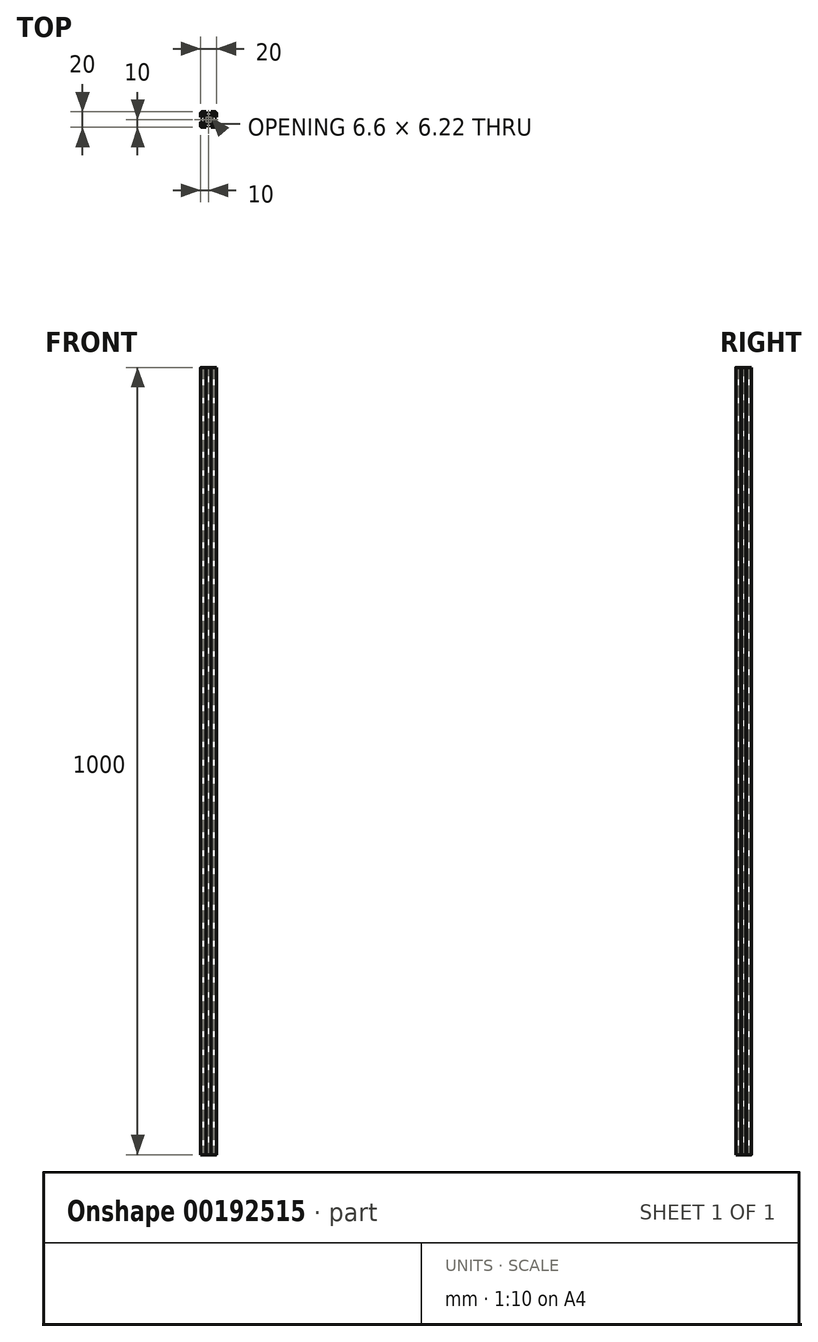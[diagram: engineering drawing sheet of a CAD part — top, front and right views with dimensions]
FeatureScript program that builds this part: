
annotation { "Feature Type Name" : "Feature", "Feature Type Description" : "" }
export const myFeature = defineFeature(function(context is Context, id is Id, definition is map)
    precondition{}
    {
        {
            var Q0;
            Q0=qCreatedBy(makeId("Top.planeOp"),FACE);
            var sketch = newSketch(context, id + "F0", { "sketchPlane" : qUnion([Q0])});
            skLineSegment(sketch, "E0.bottom", {"start": v(-10, 10) * mm, "end": v(10, 10) * mm});
            skLineSegment(sketch, "E0.top", {"start": v(-10, -10) * mm, "end": v(10, -10) * mm});
            skLineSegment(sketch, "E0.left", {"start": v(-10, 10) * mm, "end": v(-10, -10) * mm});
            skLineSegment(sketch, "E0.right", {"start": v(10, 10) * mm, "end": v(10, -10) * mm});
            skSolve(sketch);
        }
        {
            var Q0;
            Q0 = qSketchRegion(id + "F0", true);
            extrude(context, id + "F1", {"entities" : qUnion([Q0]), "depth" : 1000 * mm});
        }
        {
            var Q0;
            Q0=makeQuery(id+"F1.opExtrude","SWEPT_EDGE",EDGE,{"disambiguationData":[OSD([sQuery(id+"F0.wireOp",EDGE,"E0.bottom"),sQuery(id+"F0.wireOp",EDGE,"E0.right")])]});
            var Q1;
            Q1=makeQuery(id+"F1.opExtrude","SWEPT_EDGE",EDGE,{"disambiguationData":[OSD([sQuery(id+"F0.wireOp",EDGE,"E0.bottom"),sQuery(id+"F0.wireOp",EDGE,"E0.left")])]});
            var Q2;
            Q2=makeQuery(id+"F1.opExtrude","SWEPT_EDGE",EDGE,{"disambiguationData":[OSD([sQuery(id+"F0.wireOp",EDGE,"E0.top"),sQuery(id+"F0.wireOp",EDGE,"E0.left")])]});
            var Q3;
            Q3=makeQuery(id+"F1.opExtrude","SWEPT_EDGE",EDGE,{"disambiguationData":[OSD([sQuery(id+"F0.wireOp",EDGE,"E0.top"),sQuery(id+"F0.wireOp",EDGE,"E0.right")])]});
            fillet(context, id + "F2", {"entities" : qUnion([Q0, Q1, Q2, Q3]), "radius" : 2 * mm, "tangentPropagation" : true, "allowEdgeOverflow" : false});
        }
        {
            var Q0;
            Q0=makeQuery(id+"F1.opExtrude","CAP_FACE",FACE,{"disambiguationData":[OSD([sQuery(id+"F0.wireOp",EDGE,"E0.bottom"),sQuery(id+"F0.wireOp",EDGE,"E0.top"),sQuery(id+"F0.wireOp",EDGE,"E0.left"),sQuery(id+"F0.wireOp",EDGE,"E0.right")])],"isStart":true});
            var sketch = newSketch(context, id + "F3", { "sketchPlane" : qUnion([Q0])});
            skLineSegment(sketch, "E1", {"start": v(-10, 3) * mm, "end": v(-8.5, 3) * mm});
            skLineSegment(sketch, "E2", {"start": v(-8.5, 3) * mm, "end": v(-8.5, 5.63) * mm});
            skLineSegment(sketch, "E3", {"start": v(-8.5, 5.63) * mm, "end": v(-7.13, 5.63) * mm});
            skLineSegment(sketch, "E4", {"start": v(-7.13, 5.63) * mm, "end": v(-4.5, 3) * mm});
            skLineSegment(sketch, "E5", {"start": v(-4.5, 3) * mm, "end": v(-4.5, 0) * mm});
            skLineSegment(sketch, "E6.MirrorCS", {"start": v(-8.5, -5.63) * mm, "end": v(-7.13, -5.63) * mm});
            skLineSegment(sketch, "E7.MirrorCS", {"start": v(-10, -3) * mm, "end": v(-8.5, -3) * mm});
            skLineSegment(sketch, "E8.MirrorCS", {"start": v(-8.5, -3) * mm, "end": v(-8.5, -5.63) * mm});
            skLineSegment(sketch, "E9.MirrorCS", {"start": v(-7.13, -5.63) * mm, "end": v(-4.5, -3) * mm});
            skLineSegment(sketch, "E10.MirrorCS", {"start": v(-4.5, -3) * mm, "end": v(-4.5, 0) * mm});
            skLineSegment(sketch, "E11", {"start": v(0, 15.03) * mm, "end": v(0, -14.36) * mm, "construction": true});
            skLineSegment(sketch, "E12.MirrorCS", {"start": v(8.5, 5.63) * mm, "end": v(7.13, 5.63) * mm});
            skLineSegment(sketch, "E13.MirrorCS", {"start": v(8.5, -5.63) * mm, "end": v(7.13, -5.63) * mm});
            skLineSegment(sketch, "E14.MirrorCS", {"start": v(10, 3) * mm, "end": v(8.5, 3) * mm});
            skLineSegment(sketch, "E15.MirrorCS", {"start": v(8.5, 3) * mm, "end": v(8.5, 5.63) * mm});
            skLineSegment(sketch, "E16.MirrorCS", {"start": v(10, -3) * mm, "end": v(8.5, -3) * mm});
            skLineSegment(sketch, "E17.MirrorCS", {"start": v(7.13, 5.63) * mm, "end": v(4.5, 3) * mm});
            skLineSegment(sketch, "E18.MirrorCS", {"start": v(4.5, -3) * mm, "end": v(4.5, 0) * mm});
            skLineSegment(sketch, "E19.MirrorCS", {"start": v(7.13, -5.63) * mm, "end": v(4.5, -3) * mm});
            skLineSegment(sketch, "E20.MirrorCS", {"start": v(4.5, 3) * mm, "end": v(4.5, 0) * mm});
            skLineSegment(sketch, "E21.MirrorCS", {"start": v(8.5, -3) * mm, "end": v(8.5, -5.63) * mm});
            skLineSegment(sketch, "E22", {"start": v(-9.41, 9.41) * mm, "end": v(3, -3) * mm, "construction": true});
            skLineSegment(sketch, "E23.MirrorCS", {"start": v(-5.63, -8.5) * mm, "end": v(-5.63, -7.13) * mm});
            skLineSegment(sketch, "E24.MirrorCS", {"start": v(5.63, -8.5) * mm, "end": v(5.63, -7.13) * mm});
            skLineSegment(sketch, "E25.MirrorCS", {"start": v(-3, -10) * mm, "end": v(-3, -8.5) * mm});
            skLineSegment(sketch, "E26.MirrorCS", {"start": v(3, -10) * mm, "end": v(3, -8.5) * mm});
            skLineSegment(sketch, "E27.MirrorCS", {"start": v(-5.63, -7.13) * mm, "end": v(-3, -4.5) * mm});
            skLineSegment(sketch, "E28.MirrorCS", {"start": v(-3, -8.5) * mm, "end": v(-5.63, -8.5) * mm});
            skLineSegment(sketch, "E29.MirrorCS", {"start": v(3, -8.5) * mm, "end": v(5.63, -8.5) * mm});
            skLineSegment(sketch, "E30.MirrorCS", {"start": v(3, -4.5) * mm, "end": v(0, -4.5) * mm});
            skLineSegment(sketch, "E31.MirrorCS", {"start": v(-3, -4.5) * mm, "end": v(0, -4.5) * mm});
            skLineSegment(sketch, "E32.MirrorCS", {"start": v(5.63, -7.13) * mm, "end": v(3, -4.5) * mm});
            skLineSegment(sketch, "E33.MirrorCS", {"start": v(-15.03, 0) * mm, "end": v(14.36, 0) * mm, "construction": true});
            skLineSegment(sketch, "E34.MirrorCS", {"start": v(5.63, 7.13) * mm, "end": v(3, 4.5) * mm});
            skLineSegment(sketch, "E35.MirrorCS", {"start": v(-5.63, 7.13) * mm, "end": v(-3, 4.5) * mm});
            skLineSegment(sketch, "E36.MirrorCS", {"start": v(-3, 4.5) * mm, "end": v(0, 4.5) * mm});
            skLineSegment(sketch, "E37.MirrorCS", {"start": v(3, 4.5) * mm, "end": v(0, 4.5) * mm});
            skLineSegment(sketch, "E38.MirrorCS", {"start": v(-5.63, 8.5) * mm, "end": v(-5.63, 7.13) * mm});
            skLineSegment(sketch, "E39.MirrorCS", {"start": v(5.63, 8.5) * mm, "end": v(5.63, 7.13) * mm});
            skLineSegment(sketch, "E40.MirrorCS", {"start": v(3, 10) * mm, "end": v(3, 8.5) * mm});
            skLineSegment(sketch, "E41.MirrorCS", {"start": v(-3, 10) * mm, "end": v(-3, 8.5) * mm});
            skLineSegment(sketch, "E42.MirrorCS", {"start": v(3, 8.5) * mm, "end": v(5.63, 8.5) * mm});
            skLineSegment(sketch, "E43.MirrorCS", {"start": v(-3, 8.5) * mm, "end": v(-5.63, 8.5) * mm});
            skSolve(sketch);
        }
        {
            var Q0;
            Q0 = qSketchRegion(id + "F3", true);
            var Q1;
            Q1=makeQuery(id+"F3.imprint","IMPRINT",FACE,{"disambiguationData":[TD([[makeQuery(id+"F3.imprint","IMPRINT",EDGE,{"derivedFrom":sQuery(id+"F3.wireOp",EDGE,"E35.MirrorCS")}),1.0]])]});
            var Q2;
            Q2=makeQuery(id+"F3.imprint","IMPRINT",FACE,{"disambiguationData":[TD([[makeQuery(id+"F3.imprint","IMPRINT",EDGE,{"derivedFrom":sQuery(id+"F3.wireOp",EDGE,"E20.MirrorCS")}),1.0]])]});
            var Q3;
            Q3=makeQuery(id+"F3.imprint","IMPRINT",FACE,{"disambiguationData":[TD([[makeQuery(id+"F3.imprint","IMPRINT",EDGE,{"derivedFrom":sQuery(id+"F3.wireOp",EDGE,"E23.MirrorCS")}),-1.0]])]});
            var Q4;
            {var subQ0=sQuery(id+"F3.wireOp",EDGE,"E1");Q4=makeQuery(id+"F3.imprint","IMPRINT",FACE,{"disambiguationData":[TD([[makeQuery(id+"F3.imprint","IMPRINT",EDGE,{"derivedFrom":subQ0}),-1.0]])]});}
            extrude(context, id + "F4", {"entities" : qUnion([Q0, Q1, Q2, Q3, Q4]), "operationType" : NewBodyOperationType.REMOVE, "endBound" : BoundingType.UP_TO_NEXT, "oppositeDirection" : true, "depth" : 25.4 * mm});
        }
        {
            var Q0;
            Q0=makeQuery(id+"F1.opExtrude","CAP_FACE",FACE,{"disambiguationData":[OSD([sQuery(id+"F0.wireOp",EDGE,"E0.bottom"),sQuery(id+"F0.wireOp",EDGE,"E0.top"),sQuery(id+"F0.wireOp",EDGE,"E0.left"),sQuery(id+"F0.wireOp",EDGE,"E0.right")])],"isStart":false});
            var sketch = newSketch(context, id + "F5", { "sketchPlane" : qUnion([Q0])});
            skArc(sketch, "E44", {"start": v(-2.68, -0.6) * mm, "mid": v(-2.38, -1.37) * mm, "end": v(-1.87, -2.02) * mm});
            skLineSegment(sketch, "E45", {"start": v(-7.32, 0) * mm, "end": v(15.13, 0) * mm, "construction": true});
            skPoint(sketch, "E45.endSnap0", {"position": v(-4.5, 0) * mm});
            skLineSegment(sketch, "E46", {"start": v(-3.3, 0.5) * mm, "end": v(-3.3, 0) * mm});
            skLineSegment(sketch, "E47", {"start": v(-3.3, 0.5) * mm, "end": v(-2.68, 0.6) * mm});
            skLineSegment(sketch, "E48.MirrorCS", {"start": v(-3.3, -0.5) * mm, "end": v(-2.68, -0.6) * mm});
            skLineSegment(sketch, "E49.MirrorCS", {"start": v(-3.3, -0.5) * mm, "end": v(-3.3, 0) * mm});
            skLineSegment(sketch, "E50", {"start": v(0, 3.17) * mm, "end": v(0, -3.5) * mm, "construction": true});
            skLineSegment(sketch, "E51.MirrorCS", {"start": v(3.3, -0.5) * mm, "end": v(2.68, -0.6) * mm});
            skLineSegment(sketch, "E52.MirrorCS", {"start": v(3.3, -0.5) * mm, "end": v(3.3, 0) * mm});
            skLineSegment(sketch, "E53.MirrorCS", {"start": v(3.3, 0.5) * mm, "end": v(2.68, 0.6) * mm});
            skLineSegment(sketch, "E54.MirrorCS", {"start": v(3.3, 0.5) * mm, "end": v(3.3, 0) * mm});
            skArc(sketch, "E55.trimOffspring", {"start": v(2.68, 0.6) * mm, "mid": v(2.38, 1.38) * mm, "end": v(1.87, 2.02) * mm});
            skLineSegment(sketch, "E56", {"start": v(-2.57, 4.46) * mm, "end": v(0, 0) * mm, "construction": true});
            skLineSegment(sketch, "E57", {"start": v(0, 0) * mm, "end": v(2.15, 3.72) * mm, "construction": true});
            skLineSegment(sketch, "E58.MirrorCS", {"start": v(-2.08, 2.6) * mm, "end": v(-1.87, 2.02) * mm});
            skLineSegment(sketch, "E59.MirrorCS", {"start": v(-2.08, 2.6) * mm, "end": v(-1.65, 2.86) * mm});
            skLineSegment(sketch, "E60.MirrorCS", {"start": v(-1.22, 3.1) * mm, "end": v(-0.81, 2.63) * mm});
            skLineSegment(sketch, "E61.MirrorCS", {"start": v(-1.22, 3.1) * mm, "end": v(-1.65, 2.86) * mm});
            skLineSegment(sketch, "E62.MirrorCS", {"start": v(2.08, -2.6) * mm, "end": v(1.87, -2.02) * mm});
            skLineSegment(sketch, "E63.MirrorCS", {"start": v(5.15, 0) * mm, "end": v(0, 0) * mm, "construction": true});
            skLineSegment(sketch, "E64.MirrorCS", {"start": v(1.22, -3.1) * mm, "end": v(0.81, -2.63) * mm});
            skLineSegment(sketch, "E65.MirrorCS", {"start": v(1.22, -3.1) * mm, "end": v(1.65, -2.86) * mm});
            skLineSegment(sketch, "E66.MirrorCS", {"start": v(2.08, -2.6) * mm, "end": v(1.65, -2.86) * mm});
            skLineSegment(sketch, "E67.MirrorCS", {"start": v(2.08, 2.6) * mm, "end": v(1.87, 2.02) * mm});
            skLineSegment(sketch, "E68.MirrorCS", {"start": v(2.08, 2.6) * mm, "end": v(1.65, 2.86) * mm});
            skLineSegment(sketch, "E69.MirrorCS", {"start": v(1.22, 3.1) * mm, "end": v(0.81, 2.63) * mm});
            skLineSegment(sketch, "E70.MirrorCS", {"start": v(1.22, 3.1) * mm, "end": v(1.65, 2.86) * mm});
            skLineSegment(sketch, "E71.MirrorCS", {"start": v(-2.08, -2.6) * mm, "end": v(-1.65, -2.86) * mm});
            skLineSegment(sketch, "E72.MirrorCS", {"start": v(-1.22, -3.1) * mm, "end": v(-1.65, -2.86) * mm});
            skLineSegment(sketch, "E73.MirrorCS", {"start": v(-2.08, -2.6) * mm, "end": v(-1.87, -2.02) * mm});
            skLineSegment(sketch, "E74.MirrorCS", {"start": v(-1.22, -3.1) * mm, "end": v(-0.81, -2.63) * mm});
            skArc(sketch, "E75.trimOffspring", {"start": v(-1.87, 2.02) * mm, "mid": v(-2.38, 1.37) * mm, "end": v(-2.68, 0.6) * mm});
            skArc(sketch, "E76.trimOffspring", {"start": v(0.81, 2.63) * mm, "mid": v(0, 2.75) * mm, "end": v(-0.81, 2.63) * mm});
            skArc(sketch, "E77.trimOffspring", {"start": v(1.87, -2.02) * mm, "mid": v(2.38, -1.37) * mm, "end": v(2.68, -0.6) * mm});
            skArc(sketch, "E78.trimOffspring", {"start": v(-0.81, -2.63) * mm, "mid": v(0, -2.75) * mm, "end": v(0.81, -2.63) * mm});
            skSolve(sketch);
        }
        {
            var Q0;
            Q0 = qSketchRegion(id + "F5", true);
            extrude(context, id + "F6", {"entities" : qUnion([Q0]), "operationType" : NewBodyOperationType.REMOVE, "endBound" : BoundingType.UP_TO_NEXT, "oppositeDirection" : true, "depth" : 25.4 * mm});
        }
        {
            var Q0;
            Q0=makeQuery(id+"F1.opExtrude","CAP_FACE",FACE,{"disambiguationData":[OSD([sQuery(id+"F0.wireOp",EDGE,"E0.bottom"),sQuery(id+"F0.wireOp",EDGE,"E0.top"),sQuery(id+"F0.wireOp",EDGE,"E0.left"),sQuery(id+"F0.wireOp",EDGE,"E0.right")])],"isStart":true});
            var sketch = newSketch(context, id + "F7", { "sketchPlane" : qUnion([Q0])});
            skLineSegment(sketch, "E79.bottom", {"start": v(-10, 3) * mm, "end": v(-9.75, 3) * mm});
            skLineSegment(sketch, "E79.top", {"start": v(-10, 3.25) * mm, "end": v(-9.75, 3.25) * mm});
            skLineSegment(sketch, "E79.left", {"start": v(-10, 3) * mm, "end": v(-10, 3.25) * mm});
            skLineSegment(sketch, "E79.right", {"start": v(-9.75, 3) * mm, "end": v(-9.75, 3.25) * mm});
            skLineSegment(sketch, "E80", {"start": v(0, 12.33) * mm, "end": v(0, -11.82) * mm, "construction": true});
            skLineSegment(sketch, "E81", {"start": v(-12.76, 0) * mm, "end": v(11.5, 0) * mm, "construction": true});
            skLineSegment(sketch, "E82", {"start": v(-10, 10) * mm, "end": v(10.81, -10.81) * mm, "construction": true});
            skLineSegment(sketch, "E83", {"start": v(-9.41, -9.41) * mm, "end": v(9.41, 9.41) * mm, "construction": true});
            skLineSegment(sketch, "E84.MirrorCS", {"start": v(-3.25, 10) * mm, "end": v(-3.25, 9.75) * mm});
            skLineSegment(sketch, "E85.MirrorCS", {"start": v(-3, 10) * mm, "end": v(-3, 9.75) * mm});
            skLineSegment(sketch, "E86.MirrorCS", {"start": v(-3, 9.75) * mm, "end": v(-3.25, 9.75) * mm});
            skLineSegment(sketch, "E87.MirrorCS", {"start": v(-3, 10) * mm, "end": v(-3.25, 10) * mm});
            skLineSegment(sketch, "E88.MirrorCS", {"start": v(3.25, 10) * mm, "end": v(3.25, 9.75) * mm});
            skLineSegment(sketch, "E89.MirrorCS", {"start": v(3, 10) * mm, "end": v(3, 9.75) * mm});
            skLineSegment(sketch, "E90.MirrorCS", {"start": v(3, 10) * mm, "end": v(3.25, 10) * mm});
            skLineSegment(sketch, "E91.MirrorCS", {"start": v(3, 9.75) * mm, "end": v(3.25, 9.75) * mm});
            skLineSegment(sketch, "E92.MirrorCS", {"start": v(10, 3.25) * mm, "end": v(9.75, 3.25) * mm});
            skLineSegment(sketch, "E93.MirrorCS", {"start": v(10, 3) * mm, "end": v(10, 3.25) * mm});
            skLineSegment(sketch, "E94.MirrorCS", {"start": v(9.75, 3) * mm, "end": v(9.75, 3.25) * mm});
            skLineSegment(sketch, "E95.MirrorCS", {"start": v(10, 3) * mm, "end": v(9.75, 3) * mm});
            skLineSegment(sketch, "E96.MirrorCS", {"start": v(-10, -3.25) * mm, "end": v(-9.75, -3.25) * mm});
            skLineSegment(sketch, "E97.MirrorCS", {"start": v(-10, -3) * mm, "end": v(-10, -3.25) * mm});
            skLineSegment(sketch, "E98.MirrorCS", {"start": v(-9.75, -3) * mm, "end": v(-9.75, -3.25) * mm});
            skLineSegment(sketch, "E99.MirrorCS", {"start": v(-10, -3) * mm, "end": v(-9.75, -3) * mm});
            skLineSegment(sketch, "E100.MirrorCS", {"start": v(10, -3.25) * mm, "end": v(9.75, -3.25) * mm});
            skLineSegment(sketch, "E101.MirrorCS", {"start": v(10, -3) * mm, "end": v(10, -3.25) * mm});
            skLineSegment(sketch, "E102.MirrorCS", {"start": v(10, -3) * mm, "end": v(9.75, -3) * mm});
            skLineSegment(sketch, "E103.MirrorCS", {"start": v(9.75, -3) * mm, "end": v(9.75, -3.25) * mm});
            skLineSegment(sketch, "E104.MirrorCS", {"start": v(-3.25, -10) * mm, "end": v(-3.25, -9.75) * mm});
            skLineSegment(sketch, "E105.MirrorCS", {"start": v(-3, -10) * mm, "end": v(-3, -9.75) * mm});
            skLineSegment(sketch, "E106.MirrorCS", {"start": v(3, -10) * mm, "end": v(3.25, -10) * mm});
            skLineSegment(sketch, "E107.MirrorCS", {"start": v(-3, -9.75) * mm, "end": v(-3.25, -9.75) * mm});
            skLineSegment(sketch, "E108.MirrorCS", {"start": v(-3, -10) * mm, "end": v(-3.25, -10) * mm});
            skLineSegment(sketch, "E109.MirrorCS", {"start": v(3, -10) * mm, "end": v(3, -9.75) * mm});
            skLineSegment(sketch, "E110.MirrorCS", {"start": v(3.25, -10) * mm, "end": v(3.25, -9.75) * mm});
            skLineSegment(sketch, "E111.MirrorCS", {"start": v(3, -9.75) * mm, "end": v(3.25, -9.75) * mm});
            skSolve(sketch);
        }
        {
            var Q0;
            Q0 = qSketchRegion(id + "F7", true);
            extrude(context, id + "F8", {"entities" : qUnion([Q0]), "operationType" : NewBodyOperationType.REMOVE, "endBound" : BoundingType.UP_TO_NEXT, "oppositeDirection" : true, "depth" : 25.4 * mm});
        }
        {
            var Q0;
            Q0=makeQuery(id+"F4.boolean.opBoolean","COPY",EDGE,{"derivedFrom":makeQuery(id+"F4.opExtrude","SWEPT_EDGE",EDGE,{"disambiguationData":[OSD([sQuery(id+"F3.wireOp",EDGE,"E7.MirrorCS"),sQuery(id+"F3.wireOp",EDGE,"E8.MirrorCS")])]})});
            var Q1;
            Q1=makeQuery(id+"F4.boolean.opBoolean","COPY",EDGE,{"derivedFrom":makeQuery(id+"F4.opExtrude","SWEPT_EDGE",EDGE,{"disambiguationData":[OSD([sQuery(id+"F3.wireOp",EDGE,"E1"),sQuery(id+"F3.wireOp",EDGE,"E2")])]})});
            var Q2;
            Q2=makeQuery(id+"F4.boolean.opBoolean","COPY",EDGE,{"derivedFrom":makeQuery(id+"F4.opExtrude","SWEPT_EDGE",EDGE,{"disambiguationData":[OSD([sQuery(id+"F3.wireOp",EDGE,"E41.MirrorCS"),sQuery(id+"F3.wireOp",EDGE,"E43.MirrorCS")])]})});
            var Q3;
            Q3=makeQuery(id+"F4.boolean.opBoolean","COPY",EDGE,{"derivedFrom":makeQuery(id+"F4.opExtrude","SWEPT_EDGE",EDGE,{"disambiguationData":[OSD([sQuery(id+"F3.wireOp",EDGE,"E40.MirrorCS"),sQuery(id+"F3.wireOp",EDGE,"E42.MirrorCS")])]})});
            var Q4;
            Q4=makeQuery(id+"F4.boolean.opBoolean","COPY",EDGE,{"derivedFrom":makeQuery(id+"F4.opExtrude","SWEPT_EDGE",EDGE,{"disambiguationData":[OSD([sQuery(id+"F3.wireOp",EDGE,"E14.MirrorCS"),sQuery(id+"F3.wireOp",EDGE,"E15.MirrorCS")])]})});
            var Q5;
            Q5=makeQuery(id+"F4.boolean.opBoolean","COPY",EDGE,{"derivedFrom":makeQuery(id+"F4.opExtrude","SWEPT_EDGE",EDGE,{"disambiguationData":[OSD([sQuery(id+"F3.wireOp",EDGE,"E25.MirrorCS"),sQuery(id+"F3.wireOp",EDGE,"E28.MirrorCS")])]})});
            var Q6;
            Q6=makeQuery(id+"F4.boolean.opBoolean","COPY",EDGE,{"derivedFrom":makeQuery(id+"F4.opExtrude","SWEPT_EDGE",EDGE,{"disambiguationData":[OSD([sQuery(id+"F3.wireOp",EDGE,"E26.MirrorCS"),sQuery(id+"F3.wireOp",EDGE,"E29.MirrorCS")])]})});
            var Q7;
            Q7=makeQuery(id+"F4.boolean.opBoolean","COPY",EDGE,{"derivedFrom":makeQuery(id+"F4.opExtrude","SWEPT_EDGE",EDGE,{"disambiguationData":[OSD([sQuery(id+"F3.wireOp",EDGE,"E16.MirrorCS"),sQuery(id+"F3.wireOp",EDGE,"E21.MirrorCS")])]})});
            fillet(context, id + "F9", {"entities" : qUnion([Q0, Q1, Q2, Q3, Q4, Q5, Q6, Q7]), "radius" : 0.25 * mm, "tangentPropagation" : true, "allowEdgeOverflow" : false});
        }
    });
